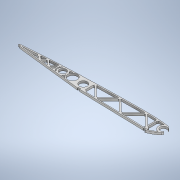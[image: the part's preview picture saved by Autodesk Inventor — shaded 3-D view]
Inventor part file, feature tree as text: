
AUTODESK INVENTOR PART (.ipt)
format: ipt  version: 2022 (Build 260153000, 153)  size: 449,536 bytes
history: native  units: mm
features: extrude x1, sketch x1
ambient origin geometry x8: Origin, YZ Plane, XZ Plane, XY Plane, X Axis, Y Axis, Z Axis, Center Point
bodies: Body1 (feature_tree)
feature tree (2):
  extrude  "Extrusion5"  Depth=10.0mm
  sketch  "Sketch1"  dims[d31=34.456mm d50=368.759386mm d57=16.0mm d69=8.0mm d70=23.0mm d71=8.0mm d73=16.0mm d80=19.0mm d81=16.0mm d82=1.0mm d83=1.0mm d84=1.0mm d85=1.0mm d86=1.0mm d87=0.8mm d88=1.0mm d90=19.0mm d94=5.0mm d95=5.0mm d105=5.0mm d106=5.0mm d108=2.0mm d109=19.0mm d114=5.0mm d115=5.0mm d116=24.0mm d117=2.5mm d118=2.5mm d123=2.5mm d124=2.5mm d125=10.0mm d126=24.0mm d127=24.0mm d128=27.0mm d135=0.5mm d136=45.0deg d139=7.0mm d165=45.0deg d169=27.0mm d175=90.0deg d181=45.0deg d185=7.0mm d186=45.0deg d190=7.0mm d191=45.0deg d197=90.0deg d203=90.0deg d206=7.0mm d207=5.0mm d208=0.0mm]
